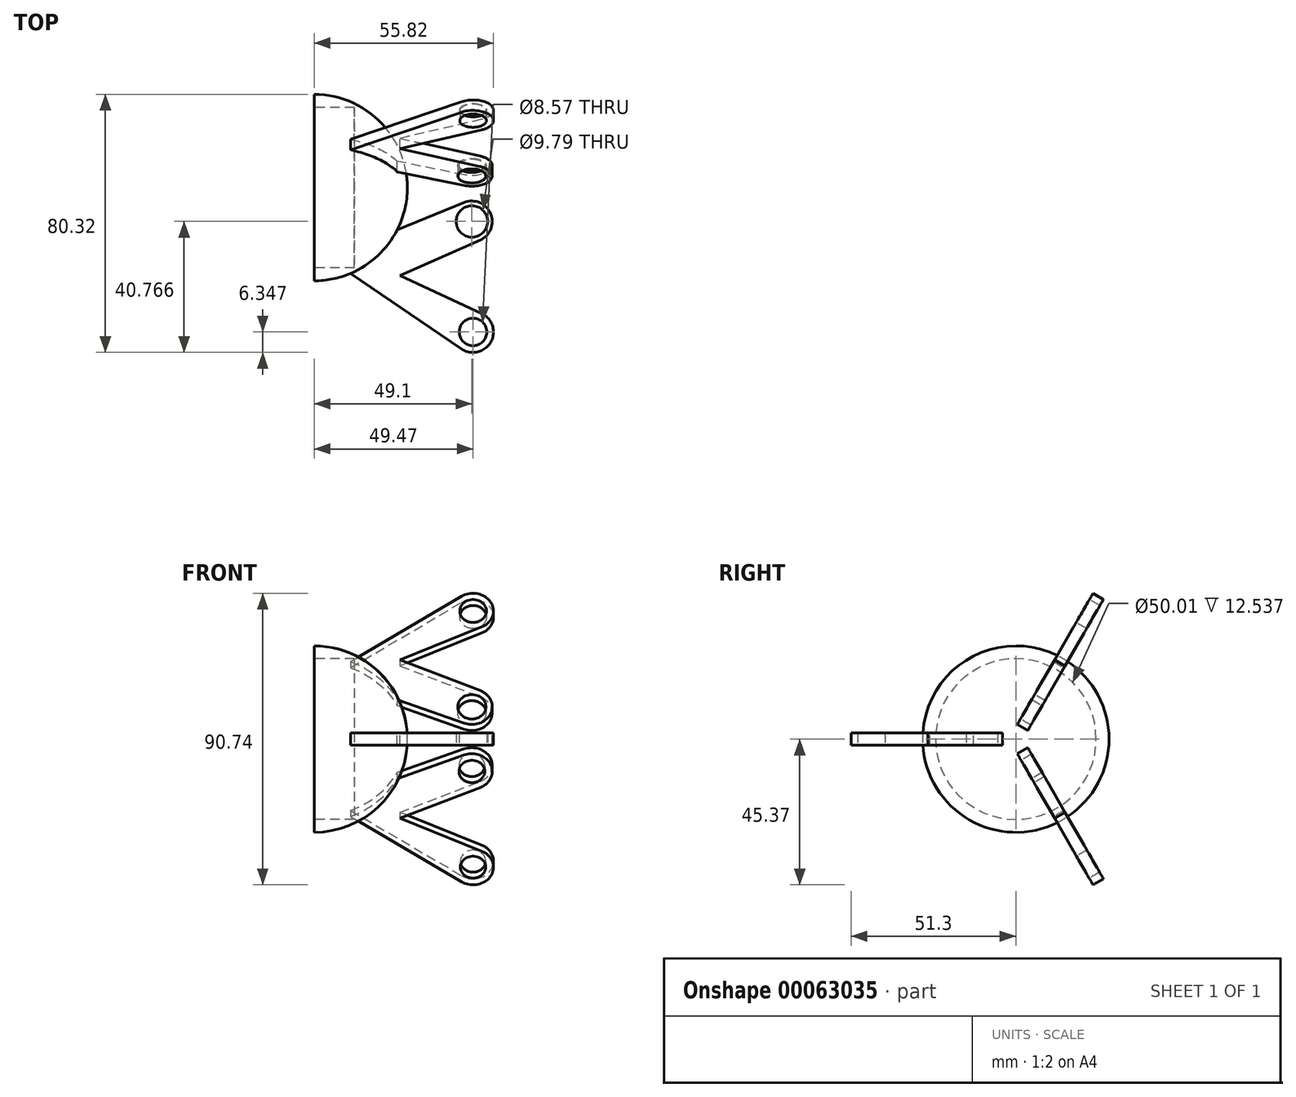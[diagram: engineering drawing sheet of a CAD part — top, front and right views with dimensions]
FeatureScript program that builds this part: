
annotation { "Feature Type Name" : "Feature", "Feature Type Description" : "" }
export const myFeature = defineFeature(function(context is Context, id is Id, definition is map)
    precondition{}
    {
        {
            var Q0;
            Q0=qCreatedBy(makeId("Front.planeOp"),FACE);
            var sketch = newSketch(context, id + "F0", { "sketchPlane" : qUnion([Q0])});
            skArc(sketch, "E0", {"start": v(29.02, 0) * mm, "mid": v(20.52, 20.52) * mm, "end": v(0, 29.02) * mm});
            skArc(sketch, "E1", {"start": v(21.53, 0) * mm, "mid": v(15.22, 15.22) * mm, "end": v(0, 21.53) * mm});
            skLineSegment(sketch, "E2", {"start": v(0, 0) * mm, "end": v(29.02, 0) * mm});
            skLineSegment(sketch, "E3", {"start": v(0, 29.02) * mm, "end": v(0, 0) * mm});
            skPoint(sketch, "E4.orphan", {"position": v(-29.02, 0) * mm});
            skSolve(sketch);
        }
        {
            var Q0;
            {var subQ0=sQuery(id+"F0.wireOp",EDGE,"E1");Q0=makeQuery(id+"F0.imprint","IMPRINT",FACE,{"disambiguationData":[TD([[makeQuery(id+"F0.imprint","IMPRINT",EDGE,{"derivedFrom":subQ0}),1.0]])]});}
            var Q1;
            {var subQ0=sQuery(id+"F0.wireOp",EDGE,"E0");Q1=makeQuery(id+"F0.imprint","IMPRINT",FACE,{"disambiguationData":[TD([[makeQuery(id+"F0.imprint","IMPRINT",EDGE,{"derivedFrom":subQ0}),1.0]])]});}
            var Q2;
            Q2=sQuery(id+"F0.wireOp",EDGE,"E2");
            revolve(context, id + "F1", {"entities" : qUnion([Q0, Q1]), "axis" : qUnion([Q2]), "revolveType" : RevolveType.FULL});
        }
        {
            var Q0;
            Q0=makeQuery(id+"F1.opRevolve","SWEPT_FACE",FACE,{"disambiguationData":[OSD([sQuery(id+"F0.wireOp",EDGE,"E3")])]});
            var sketch = newSketch(context, id + "F2", { "sketchPlane" : qUnion([Q0])});
            skCircle(sketch, "E5", {"center": v(0, 0) * mm, "radius": 25 * mm});
            skSolve(sketch);
        }
        {
            var Q0;
            Q0 = qSketchRegion(id + "F2", true);
            extrude(context, id + "F3", {"entities" : qUnion([Q0]), "operationType" : NewBodyOperationType.REMOVE, "oppositeDirection" : true, "depth" : 12.54 * mm});
        }
        {
            var Q0;
            Q0=qCreatedBy(makeId("Top.planeOp"),FACE);
            var sketch = newSketch(context, id + "F4", { "sketchPlane" : qUnion([Q0])});
            skLineSegment(sketch, "E6", {"start": v(11.3, -26.73) * mm, "end": v(45.9, -50.2) * mm});
            skLineSegment(sketch, "E7", {"start": v(52.14, -39.2) * mm, "end": v(26.72, -27.4) * mm});
            skLineSegment(sketch, "E8", {"start": v(26.72, -27.4) * mm, "end": v(51.67, -16.34) * mm});
            skLineSegment(sketch, "E9", {"start": v(46.7, -4.65) * mm, "end": v(25.88, -13.13) * mm});
            skPoint(sketch, "E10.visualSharp", {"position": v(-18.73, -6.34) * mm});
            skArc(sketch, "E10.filletArc", {"start": v(45.9, -50.2) * mm, "mid": v(55, -48.08) * mm, "end": v(52.14, -39.2) * mm});
            skPoint(sketch, "E11.visualSharp", {"position": v(425.55, 149.52) * mm});
            skArc(sketch, "E11.filletArc", {"start": v(51.67, -16.34) * mm, "mid": v(54.94, -8.05) * mm, "end": v(46.7, -4.65) * mm});
            skArc(sketch, "E12", {"start": v(0, 29.02) * mm, "mid": v(29.02, 0) * mm, "end": v(0, -29.02) * mm});
            skSolve(sketch);
        }
        {
            var Q0;
            Q0 = qSketchRegion(id + "F4", true);
            extrude(context, id + "F5", {"entities" : qUnion([Q0]), "endBound" : BoundingType.SYMMETRIC, "oppositeDirection" : true, "depth" : 3.76 * mm});
        }
        {
            var Q0;
            Q0=makeQuery(id+"F5.opExtrude","SWEPT_BODY",BODY,{"disambiguationData":[OSD([sQuery(id+"F4.wireOp",EDGE,"E6"),sQuery(id+"F4.wireOp",EDGE,"E7"),sQuery(id+"F4.wireOp",EDGE,"E8"),sQuery(id+"F4.wireOp",EDGE,"E9"),sQuery(id+"F4.wireOp",EDGE,"KY50rEt2-9OAX-3IGb-rHpy-M5Xas2YAmzqe")])]});
            var Q1;
            Q1=sQuery(id+"F0.wireOp",EDGE,"E2");
            circularPattern(context, id + "F6", {"entities" : qUnion([Q0]), "axis" : qUnion([Q1]), "angle" : 360 * degree, "instanceCount" : 3, "equalSpace" : true});
        }
        {
            var Q0;
            Q0=makeQuery(id+"F5.opExtrude","CAP_FACE",FACE,{"disambiguationData":[OSD([sQuery(id+"F4.wireOp",EDGE,"E6"),sQuery(id+"F4.wireOp",EDGE,"E7"),sQuery(id+"F4.wireOp",EDGE,"E8"),sQuery(id+"F4.wireOp",EDGE,"E9"),sQuery(id+"F4.wireOp",EDGE,"KY50rEt2-9OAX-3IGb-rHpy-M5Xas2YAmzqe"),sQuery(id+"F4.wireOp",EDGE,"E10.filletArc"),sQuery(id+"F4.wireOp",EDGE,"E11.filletArc")])],"isStart":false});
            var sketch = newSketch(context, id + "F7", { "sketchPlane" : qUnion([Q0])});
            skCircle(sketch, "E13", {"center": v(49.47, 44.95) * mm, "radius": 4.29 * mm});
            skCircle(sketch, "E14", {"center": v(49.1, 10.53) * mm, "radius": 4.9 * mm});
            skSolve(sketch);
        }
        {
            var Q0;
            Q0=makeQuery(id+"F6.opPattern","COPY",FACE,{"derivedFrom":makeQuery(id+"F5.opExtrude","CAP_FACE",FACE,{"disambiguationData":[OSD([sQuery(id+"F4.wireOp",EDGE,"E6"),sQuery(id+"F4.wireOp",EDGE,"E7"),sQuery(id+"F4.wireOp",EDGE,"E8"),sQuery(id+"F4.wireOp",EDGE,"E9"),sQuery(id+"F4.wireOp",EDGE,"KY50rEt2-9OAX-3IGb-rHpy-M5Xas2YAmzqe"),sQuery(id+"F4.wireOp",EDGE,"E10.filletArc"),sQuery(id+"F4.wireOp",EDGE,"E11.filletArc")])],"isStart":true}),"instanceName":"1"});
            var sketch = newSketch(context, id + "F8", { "sketchPlane" : qUnion([Q0])});
            skCircle(sketch, "E15", {"center": v(49.47, -44.95) * mm, "radius": 3.95 * mm});
            skCircle(sketch, "E16", {"center": v(49.1, -10.53) * mm, "radius": 4.02 * mm});
            skSolve(sketch);
        }
        {
            var Q0;
            Q0=makeQuery(id+"F6.opPattern","COPY",FACE,{"derivedFrom":makeQuery(id+"F5.opExtrude","CAP_FACE",FACE,{"disambiguationData":[OSD([sQuery(id+"F4.wireOp",EDGE,"E6"),sQuery(id+"F4.wireOp",EDGE,"E7"),sQuery(id+"F4.wireOp",EDGE,"E8"),sQuery(id+"F4.wireOp",EDGE,"E9"),sQuery(id+"F4.wireOp",EDGE,"KY50rEt2-9OAX-3IGb-rHpy-M5Xas2YAmzqe"),sQuery(id+"F4.wireOp",EDGE,"E10.filletArc"),sQuery(id+"F4.wireOp",EDGE,"E11.filletArc")])],"isStart":false}),"instanceName":"2"});
            var sketch = newSketch(context, id + "F9", { "sketchPlane" : qUnion([Q0])});
            skCircle(sketch, "E17", {"center": v(49.1, 10.53) * mm, "radius": 4.4 * mm});
            skCircle(sketch, "E18", {"center": v(49.47, 44.95) * mm, "radius": 4.15 * mm});
            skSolve(sketch);
        }
        {
            var Q0;
            Q0=makeQuery(id+"F7.imprint","IMPRINT",FACE,{"disambiguationData":[TD([[makeQuery(id+"F7.imprint","IMPRINT",EDGE,{"derivedFrom":sQuery(id+"F7.wireOp",EDGE,"E14")}),1.0]])]});
            var Q1;
            Q1=makeQuery(id+"F7.imprint","IMPRINT",FACE,{"disambiguationData":[TD([[makeQuery(id+"F7.imprint","IMPRINT",EDGE,{"derivedFrom":sQuery(id+"F7.wireOp",EDGE,"E13")}),1.0]])]});
            extrude(context, id + "F10", {"entities" : qUnion([Q0, Q1]), "operationType" : NewBodyOperationType.REMOVE, "oppositeDirection" : true, "depth" : 25.4 * mm});
        }
        {
            var Q0;
            Q0=makeQuery(id+"F8.imprint","IMPRINT",FACE,{"disambiguationData":[TD([[makeQuery(id+"F8.imprint","IMPRINT",EDGE,{"derivedFrom":sQuery(id+"F8.wireOp",EDGE,"E15")}),1.0]])]});
            var Q1;
            Q1=makeQuery(id+"F8.imprint","IMPRINT",FACE,{"disambiguationData":[TD([[makeQuery(id+"F8.imprint","IMPRINT",EDGE,{"derivedFrom":sQuery(id+"F8.wireOp",EDGE,"E16")}),1.0]])]});
            extrude(context, id + "F11", {"entities" : qUnion([Q0, Q1]), "operationType" : NewBodyOperationType.REMOVE, "oppositeDirection" : true, "depth" : 25.4 * mm});
        }
        {
            var Q0;
            Q0=makeQuery(id+"F9.imprint","IMPRINT",FACE,{"disambiguationData":[TD([[makeQuery(id+"F9.imprint","IMPRINT",EDGE,{"derivedFrom":sQuery(id+"F9.wireOp",EDGE,"E17")}),1.0]])]});
            var Q1;
            Q1=makeQuery(id+"F9.imprint","IMPRINT",FACE,{"disambiguationData":[TD([[makeQuery(id+"F9.imprint","IMPRINT",EDGE,{"derivedFrom":sQuery(id+"F9.wireOp",EDGE,"E18")}),1.0]])]});
            extrude(context, id + "F12", {"entities" : qUnion([Q0, Q1]), "operationType" : NewBodyOperationType.REMOVE, "oppositeDirection" : true, "depth" : 25.4 * mm});
        }
    });
